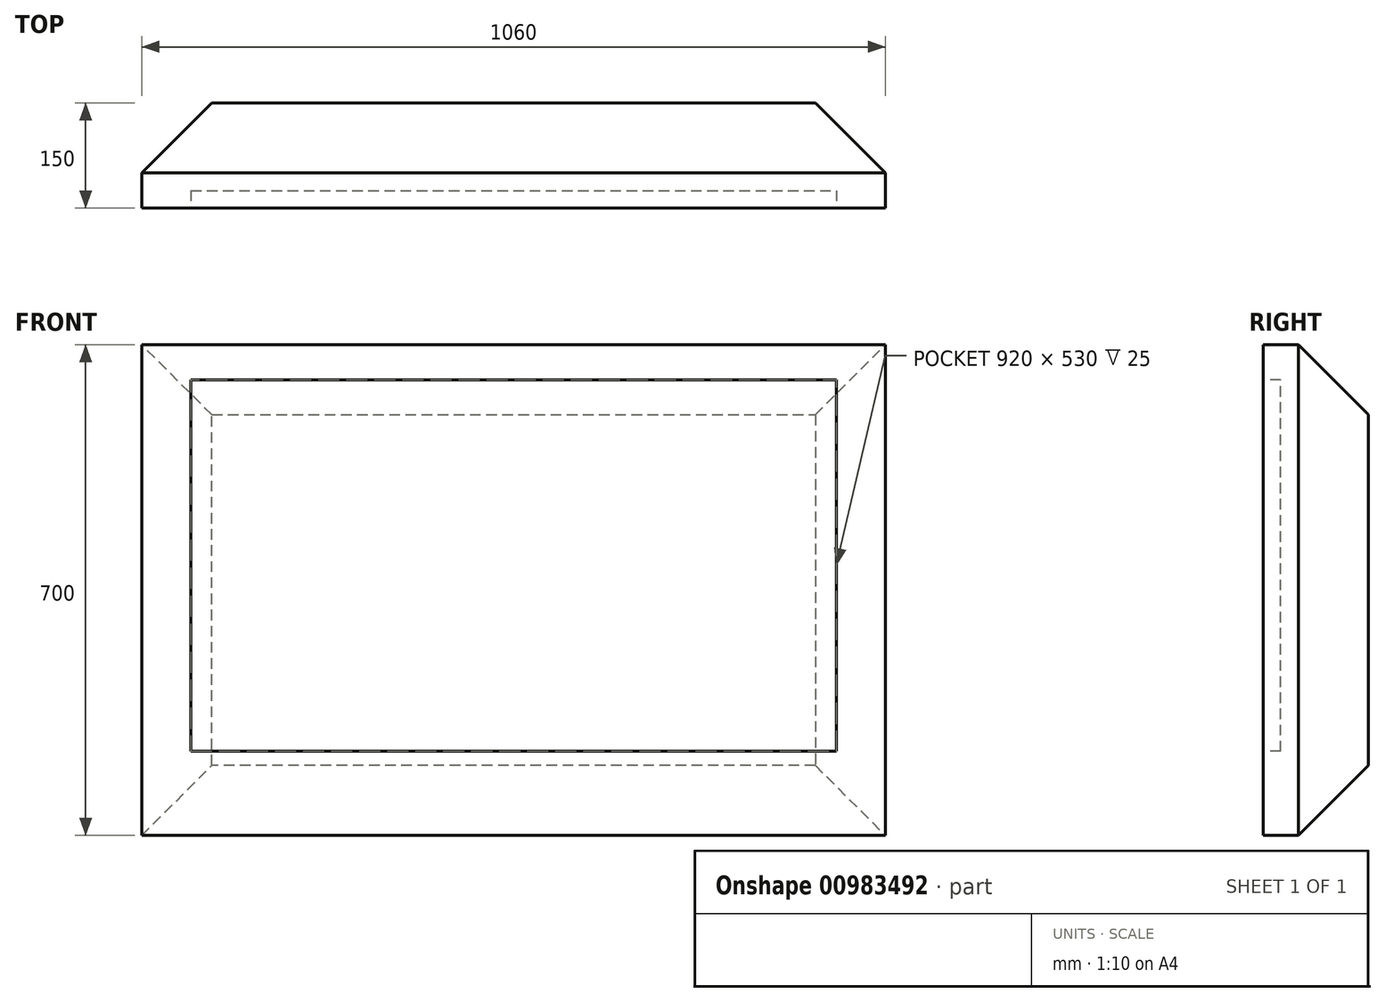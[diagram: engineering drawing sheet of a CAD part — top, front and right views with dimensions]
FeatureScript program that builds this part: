
annotation { "Feature Type Name" : "Feature", "Feature Type Description" : "" }
export const myFeature = defineFeature(function(context is Context, id is Id, definition is map)
    precondition{}
    {
        {
            var Q0;
            Q0=qCreatedBy(makeId("Front.planeOp"),FACE);
            var sketch = newSketch(context, id + "F0", { "sketchPlane" : qUnion([Q0])});
            skLineSegment(sketch, "E0.bottom", {"start": v(0, 0) * mm, "end": v(1060, 0) * mm});
            skLineSegment(sketch, "E0.top", {"start": v(0, 700) * mm, "end": v(1060, 700) * mm});
            skLineSegment(sketch, "E0.left", {"start": v(0, 0) * mm, "end": v(0, 700) * mm});
            skLineSegment(sketch, "E0.right", {"start": v(1060, 0) * mm, "end": v(1060, 700) * mm});
            skSolve(sketch);
        }
        {
            var Q0;
            Q0 = qSketchRegion(id + "F0", true);
            extrude(context, id + "F1", {"entities" : qUnion([Q0]), "depth" : 150 * mm, "offsetDistance" : 25 * mm});
        }
        {
            var Q0;
            Q0=makeQuery(id+"F1.opExtrude","CAP_EDGE",EDGE,{"disambiguationData":[OSD([sQuery(id+"F0.wireOp",EDGE,"E0.right")])],"isStart":true});
            var Q1;
            Q1=makeQuery(id+"F1.opExtrude","CAP_EDGE",EDGE,{"disambiguationData":[OSD([sQuery(id+"F0.wireOp",EDGE,"E0.top")])],"isStart":true});
            var Q2;
            Q2=makeQuery(id+"F1.opExtrude","CAP_EDGE",EDGE,{"disambiguationData":[OSD([sQuery(id+"F0.wireOp",EDGE,"E0.left")])],"isStart":true});
            var Q3;
            Q3=makeQuery(id+"F1.opExtrude","CAP_EDGE",EDGE,{"disambiguationData":[OSD([sQuery(id+"F0.wireOp",EDGE,"E0.bottom")])],"isStart":true});
            chamfer(context, id + "F2", {"entities" : qUnion([Q0, Q1, Q2, Q3]), "width" : 100 * mm, "tangentPropagation" : true});
        }
        {
            var Q0;
            Q0=makeQuery(id+"F1.opExtrude","CAP_FACE",FACE,{"disambiguationData":[OSD([sQuery(id+"F0.wireOp",EDGE,"E0.bottom"),sQuery(id+"F0.wireOp",EDGE,"E0.top"),sQuery(id+"F0.wireOp",EDGE,"E0.left"),sQuery(id+"F0.wireOp",EDGE,"E0.right")])],"isStart":false});
            var sketch = newSketch(context, id + "F3", { "sketchPlane" : qUnion([Q0])});
            skLineSegment(sketch, "E1.0", {"start": v(990, 120) * mm, "end": v(990, 650) * mm});
            skLineSegment(sketch, "E2.0", {"start": v(70, 120) * mm, "end": v(70, 650) * mm});
            skLineSegment(sketch, "E3.0", {"start": v(70, 120) * mm, "end": v(990, 120) * mm});
            skLineSegment(sketch, "E4.0", {"start": v(70, 650) * mm, "end": v(990, 650) * mm});
            skPoint(sketch, "E5.start.orphan", {"position": v(1060, 350) * mm});
            skPoint(sketch, "E6.trimOffspring.end.orphan", {"position": v(0, 350) * mm});
            skSolve(sketch);
        }
        {
            var Q0;
            Q0 = qSketchRegion(id + "F3", true);
            extrude(context, id + "F4", {"entities" : qUnion([Q0]), "operationType" : NewBodyOperationType.REMOVE, "oppositeDirection" : true, "depth" : 25 * mm, "offsetDistance" : 25 * mm});
        }
    });
